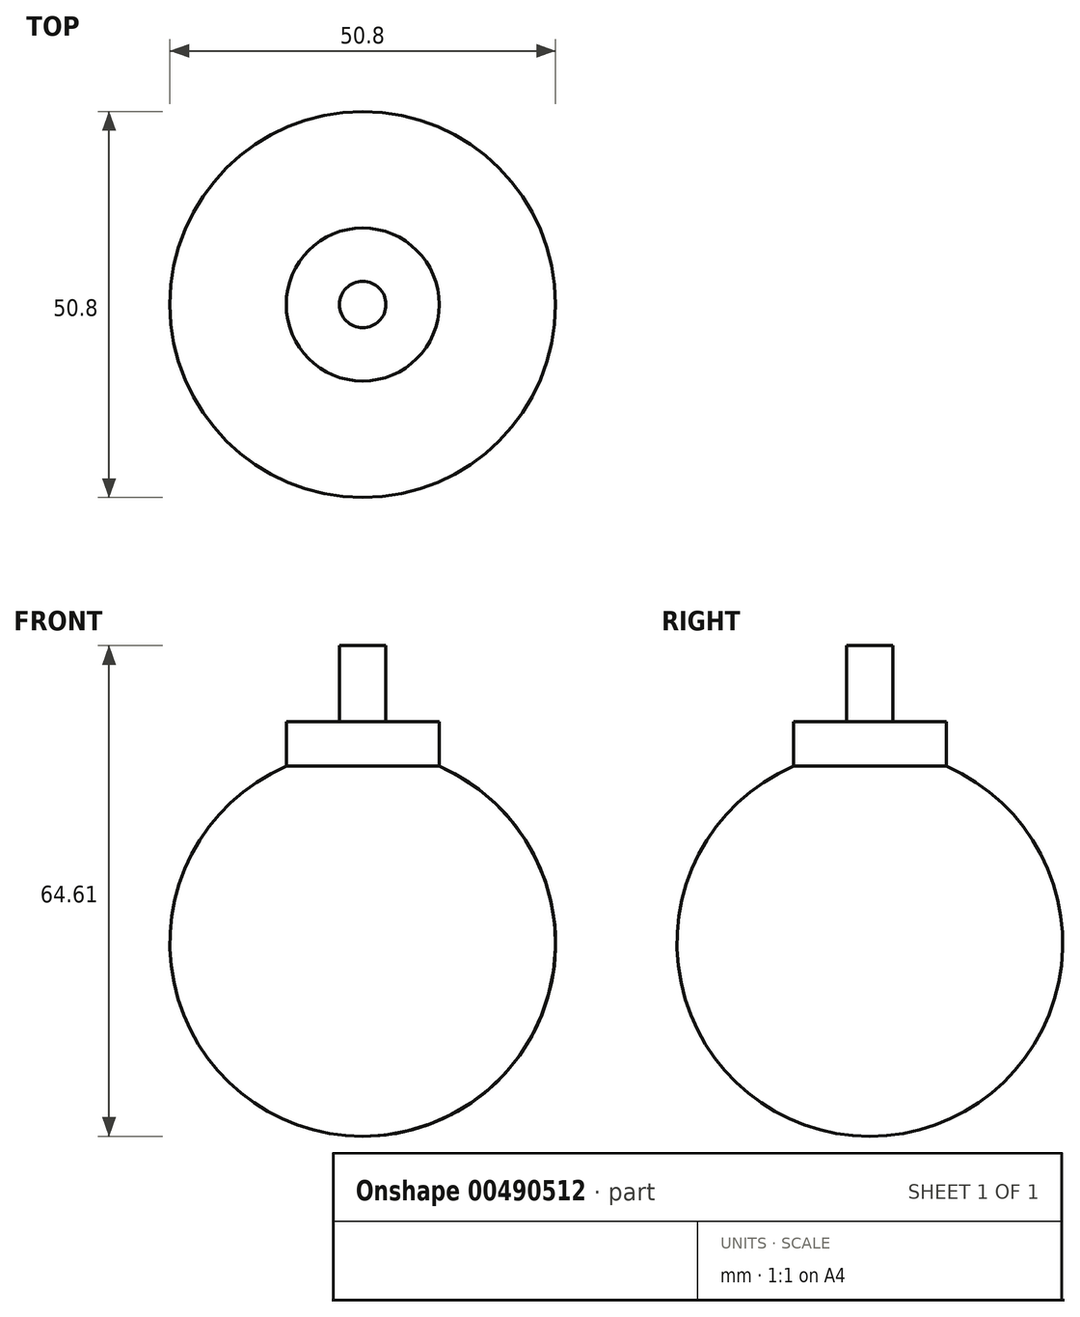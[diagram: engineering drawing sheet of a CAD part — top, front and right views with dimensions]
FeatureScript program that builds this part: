
annotation { "Feature Type Name" : "Feature", "Feature Type Description" : "" }
export const myFeature = defineFeature(function(context is Context, id is Id, definition is map)
    precondition{}
    {
        {
            var Q0;
            Q0=qCreatedBy(makeId("Top.planeOp"),FACE);
            var sketch = newSketch(context, id + "F0", { "sketchPlane" : qUnion([Q0])});
            skCircle(sketch, "E0", {"center": v(0, 0) * mm, "radius": 25.4 * mm});
            skSolve(sketch);
        }
        {
            var Q0;
            Q0 = qSketchRegion(id + "F0", true);
            extrude(context, id + "F1", {"entities" : qUnion([Q0]), "depth" : 50.8 * mm});
        }
        {
            var Q0;
            Q0=makeQuery(id+"F1.opExtrude","CAP_FACE",FACE,{"disambiguationData":[OSD([sQuery(id+"F0.wireOp",EDGE,"E0")])],"isStart":false});
            var Q1;
            Q1=makeQuery(id+"F1.opExtrude","CAP_FACE",FACE,{"disambiguationData":[OSD([sQuery(id+"F0.wireOp",EDGE,"E0")])],"isStart":true});
            fillet(context, id + "F2", {"entities" : qUnion([Q0, Q1]), "radius" : 25.4 * mm, "tangentPropagation" : true, "allowEdgeOverflow" : false});
        }
        {
            var Q0;
            Q0=qCreatedBy(makeId("Top.planeOp"),FACE);
            cPlane(context, id + "F3", {"entities" : qUnion([Q0]), "cplaneType" : CPlaneType.OFFSET, "offset" : 48.26 * mm, "width" : 152.4 * mm, "height" : 152.4 * mm});
        }
        {
            var Q0;
            Q0=qCreatedBy(id+"F3.planeOp",FACE);
            var sketch = newSketch(context, id + "F4", { "sketchPlane" : qUnion([Q0])});
            skCircle(sketch, "E1", {"center": v(0, 0) * mm, "radius": 10.08 * mm});
            skSolve(sketch);
        }
        {
            var Q0;
            Q0 = qSketchRegion(id + "F4", true);
            extrude(context, id + "F5", {"entities" : qUnion([Q0]), "operationType" : NewBodyOperationType.ADD, "depth" : 6.35 * mm});
        }
        {
            var Q0;
            Q0=makeQuery(id+"F5.opExtrude","CAP_FACE",FACE,{"disambiguationData":[OSD([sQuery(id+"F4.wireOp",EDGE,"E1")])],"isStart":false});
            cPlane(context, id + "F6", {"entities" : qUnion([Q0]), "cplaneType" : CPlaneType.OFFSET, "offset" : 0 * mm, "width" : 152.4 * mm, "height" : 152.4 * mm});
        }
        {
            var Q0;
            Q0=qCreatedBy(id+"F6.planeOp",FACE);
            var sketch = newSketch(context, id + "F7", { "sketchPlane" : qUnion([Q0])});
            skCircle(sketch, "E2", {"center": v(0, 0) * mm, "radius": 3.06 * mm});
            skSolve(sketch);
        }
        {
            var Q0;
            Q0=makeQuery(id+"F7.imprint","IMPRINT",FACE,{"disambiguationData":[TD([[makeQuery(id+"F7.imprint","IMPRINT",EDGE,{"derivedFrom":sQuery(id+"F7.wireOp",EDGE,"E2")}),1.0]])]});
            extrude(context, id + "F8", {"entities" : qUnion([Q0]), "operationType" : NewBodyOperationType.ADD, "depth" : 10 * mm});
        }
    });
